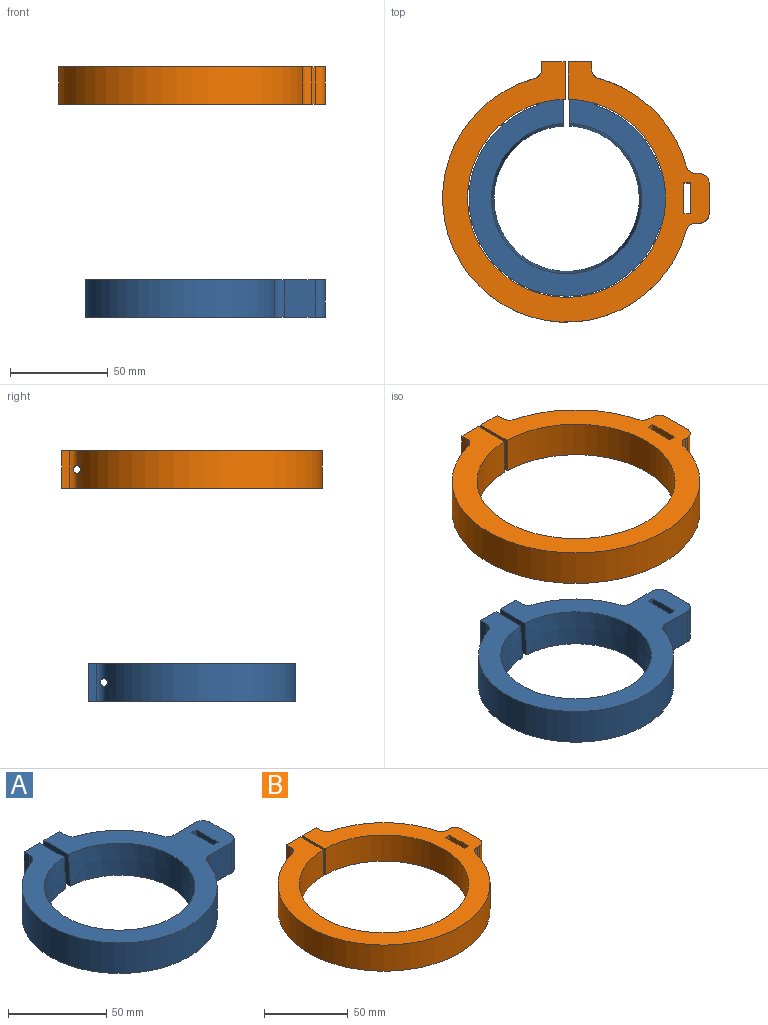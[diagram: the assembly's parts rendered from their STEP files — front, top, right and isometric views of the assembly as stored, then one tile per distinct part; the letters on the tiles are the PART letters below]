
ASSEMBLY  parts=2 mates=1
PART A: 29 faces, bbox 122.6x105.9x19.1 mm
  f0: cylinder r=49.78mm len=96.88mm, axis (0,0,-1), area 3837.6mm2, adj f2,f3,f21,f22,f25
  f1: cylinder r=2.55mm len=7.94mm, axis (1,0,0), area 127.3mm2, adj f10,f20
  f2: plane 122.57x105.92mm, normal (0,0,1), area 3812.5mm2, adj f0,f4,f5,f6,f7,f8,f9,f10
  f3: plane 122.57x105.92mm, normal (0,0,-1), area 4124.2mm2, adj f0,f4,f5,f6,f7,f8,f9,f10
  f4: cylinder r=49.78mm len=30.96mm, axis (0,0,-1), area 774.1mm2, adj f2,f3,f19,f23,f24,f28
  f5: plane 19.05x11.11mm, normal (0,1,0), area 211.7mm2, adj f2,f3,f7,f11
  f6: cone r=37.08mm half-angle=4deg, axis (0,0,1), area 4468.9mm2, adj f2,f3,f10,f11
  f7: plane 19.05x4.23mm, normal (-1,0,0), area 80.6mm2, adj f2,f3,f5,f22
  f8: plane 19.05x4.23mm, normal (1,0,0), area 70.8mm2, adj f2,f3,f9,f19,f23,f28
  f9: plane 19.05x11.11mm, normal (0,1,0), area 211.7mm2, adj f2,f3,f8,f10
  f10: plane 19.08x19.05mm, normal (-1,0,0), area 330.4mm2, adj f1,f2,f3,f6,f9
  f11: plane 19.08x19.05mm, normal (1,0,0), area 339.5mm2, adj f2,f3,f5,f6,f21
  f12: plane 19.05x15.8mm, normal (0,1,0), area 301mm2, adj f2,f3,f24,f27
  f13: plane 19.05x15.8mm, normal (0,-1,0), area 301mm2, adj f2,f3,f25,f26
  f14: plane 19.05x15.24mm, normal (1,0,0), area 290.3mm2, adj f2,f3,f26,f27
  f15: plane 19.05x3.43mm, normal (0,-1,0), area 65.3mm2, adj f2,f3,f16,f18
  f16: plane 19.05x15.62mm, normal (1,0,0), area 297.6mm2, adj f2,f3,f15,f17
  f17: plane 19.05x3.43mm, normal (0,1,0), area 65.3mm2, adj f2,f3,f16,f18
  f18: plane 19.05x15.62mm, normal (-1,0,0), area 297.6mm2, adj f2,f3,f15,f17
  f19: cylinder r=5.52mm len=16.22mm, axis (1,0,0), area 271.5mm2, adj f4,f8,f20,f23,f28
  f20: plane 11.05x11.05mm, normal (1,0,0), area 75.4mm2, adj f1,f19
  f21: cylinder r=1.9mm len=16.87mm, axis (1,0,0), area 161.1mm2, adj f0,f11,f22
  f22: cylinder r=5.08mm len=19.05mm, axis (0,0,-1), area 105.6mm2, adj f0,f2,f3,f7,f21
  f23: cylinder r=5.08mm len=5.48mm, axis (0,0,-1), area 27.1mm2, adj f3,f4,f8,f19
  f24: cylinder r=5.08mm len=19.05mm, axis (0,0,-1), area 120.1mm2, adj f2,f3,f4,f12
  f25: cylinder r=5.08mm len=19.05mm, axis (0,0,-1), area 120.1mm2, adj f0,f2,f3,f13
  f26: cylinder r=5.08mm len=19.05mm, axis (0,0,-1), area 152mm2, adj f2,f3,f13,f14
  f27: cylinder r=5.08mm len=19.05mm, axis (0,0,1), area 152mm2, adj f2,f3,f12,f14
  f28: cylinder r=5.08mm len=5.48mm, axis (0,0,-1), area 27.1mm2, adj f2,f4,f8,f19
PART B: 29 faces, bbox 136x132.8x19.1 mm
  f0: plane 136.02x132.84mm, normal (0,0,1), area 4882.4mm2, adj f2,f3,f5,f6,f7,f8,f9,f10
  f1: plane 136.02x132.84mm, normal (0,0,-1), area 4882.4mm2, adj f2,f3,f5,f6,f7,f8,f9,f10
  f2: cylinder r=63.25mm len=44.61mm, axis (0,0,-1), area 1162.2mm2, adj f0,f1,f12,f22,f27,f28
  f3: cylinder r=63.25mm len=124.31mm, axis (0,0,-1), area 5034.1mm2, adj f0,f1,f14,f23,f26
  f4: cylinder r=2.55mm len=8.73mm, axis (1,0,0), area 140mm2, adj f10,f13
  f5: plane 19.05x3.62mm, normal (1,0,0), area 64.1mm2, adj f0,f1,f8,f12,f27,f28
  f6: plane 19.05x11.91mm, normal (0,1,0), area 226.8mm2, adj f0,f1,f9,f11
  f7: cylinder r=50.55mm len=101.09mm, axis (0,0,-1), area 6019.8mm2, adj f0,f1,f10,f11
  f8: plane 19.05x11.91mm, normal (0,1,0), area 226.8mm2, adj f0,f1,f5,f10
  f9: plane 19.05x3.62mm, normal (-1,0,0), area 69mm2, adj f0,f1,f6,f26
  f10: plane 19.06x19.05mm, normal (-1,0,0), area 342.5mm2, adj f0,f1,f4,f7,f8
  f11: plane 19.06x19.05mm, normal (1,0,0), area 351.7mm2, adj f0,f1,f6,f7,f14
  f12: cylinder r=5.14mm len=18.26mm, axis (1,0,0), area 277.4mm2, adj f2,f5,f13,f27,f28
  f13: plane 10.28x10.28mm, normal (1,0,0), area 62.6mm2, adj f4,f12
  f14: cylinder r=1.9mm len=19.03mm, axis (1,0,0), area 177.2mm2, adj f3,f11,f26
  f15: plane 19.05x1.72mm, normal (0,1,0), area 32.7mm2, adj f0,f1,f22,f25
  f16: plane 19.05x1.72mm, normal (0,-1,0), area 32.7mm2, adj f0,f1,f23,f24
  f17: plane 19.05x15.24mm, normal (1,0,0), area 290.3mm2, adj f0,f1,f24,f25
  f18: plane 19.05x3.43mm, normal (0,-1,0), area 65.3mm2, adj f0,f1,f19,f21
  f19: plane 19.05x15.62mm, normal (1,0,0), area 297.6mm2, adj f0,f1,f18,f20
  f20: plane 19.05x3.43mm, normal (0,1,0), area 65.3mm2, adj f0,f1,f19,f21
  f21: plane 19.05x15.62mm, normal (-1,0,0), area 297.6mm2, adj f0,f1,f18,f20
  f22: cylinder r=5.08mm len=19.05mm, axis (0,0,-1), area 126.5mm2, adj f0,f1,f2,f15
  f23: cylinder r=5.08mm len=19.05mm, axis (0,0,-1), area 126.5mm2, adj f0,f1,f3,f16
  f24: cylinder r=5.08mm len=19.05mm, axis (0,0,-1), area 152mm2, adj f0,f1,f16,f17
  f25: cylinder r=5.08mm len=19.05mm, axis (0,0,1), area 152mm2, adj f0,f1,f15,f17
  f26: cylinder r=5.08mm len=19.05mm, axis (0,0,-1), area 111.8mm2, adj f0,f1,f3,f9,f14
  f27: cylinder r=5.08mm len=6.31mm, axis (0,0,-1), area 31.6mm2, adj f0,f2,f5,f12
  f28: cylinder r=5.08mm len=6.31mm, axis (0,0,-1), area 31.6mm2, adj f1,f2,f5,f12
PLACE A t=(16.43,7.39,-77.48)mm
PLACE B t=(16.43,7.39,31.2)mm
MATE slider B.f7 <-> A.f6  axis (0,0,1) through (16.43,7.39,50.25)mm
